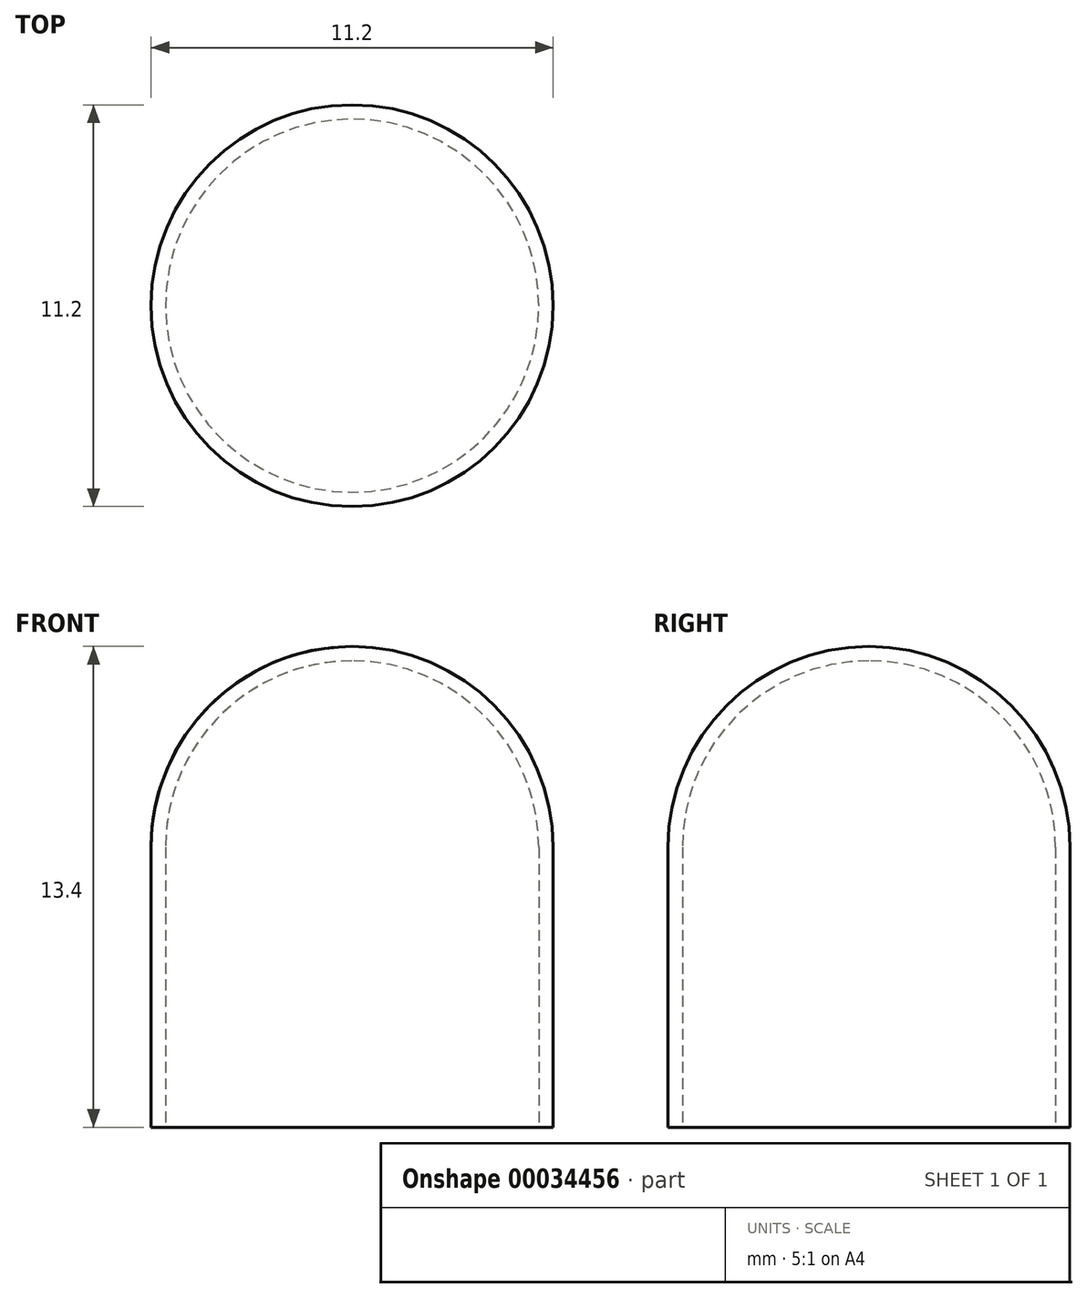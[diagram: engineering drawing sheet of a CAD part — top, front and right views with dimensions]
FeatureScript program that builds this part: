
annotation { "Feature Type Name" : "Feature", "Feature Type Description" : "" }
export const myFeature = defineFeature(function(context is Context, id is Id, definition is map)
    precondition{}
    {
        {
            var Q0;
            Q0=qCreatedBy(makeId("Front.planeOp"),FACE);
            var sketch = newSketch(context, id + "F0", { "sketchPlane" : qUnion([Q0])});
            skLineSegment(sketch, "E0", {"start": v(0, 0) * mm, "end": v(0, 19.14) * mm, "construction": true});
            skLineSegment(sketch, "E1.MirrorCS", {"start": v(-5.2, 0) * mm, "end": v(-5.2, 7.8) * mm});
            skArc(sketch, "E2.MirrorCS", {"start": v(0, 13) * mm, "mid": v(-3.68, 11.48) * mm, "end": v(-5.2, 7.8) * mm});
            skArc(sketch, "E3.2", {"start": v(0, 13.4) * mm, "mid": v(-3.96, 11.76) * mm, "end": v(-5.6, 7.8) * mm});
            skLineSegment(sketch, "E3.3", {"start": v(-5.6, 0) * mm, "end": v(-5.6, 7.8) * mm});
            skLineSegment(sketch, "E4", {"start": v(-5.2, 0) * mm, "end": v(-5.6, 0) * mm});
            skLineSegment(sketch, "E5", {"start": v(0, 13.4) * mm, "end": v(0, 10.8) * mm});
            skSolve(sketch);
        }
        {
            var Q0;
            Q0 = qSketchRegion(id + "F0", true);
            var Q1;
            Q1=sQuery(id+"F0.wireOp",EDGE,"E0");
            revolve(context, id + "F1", {"entities" : qUnion([Q0]), "axis" : qUnion([Q1]), "revolveType" : RevolveType.SYMMETRIC, "angle" : 360 * degree});
        }
    });
